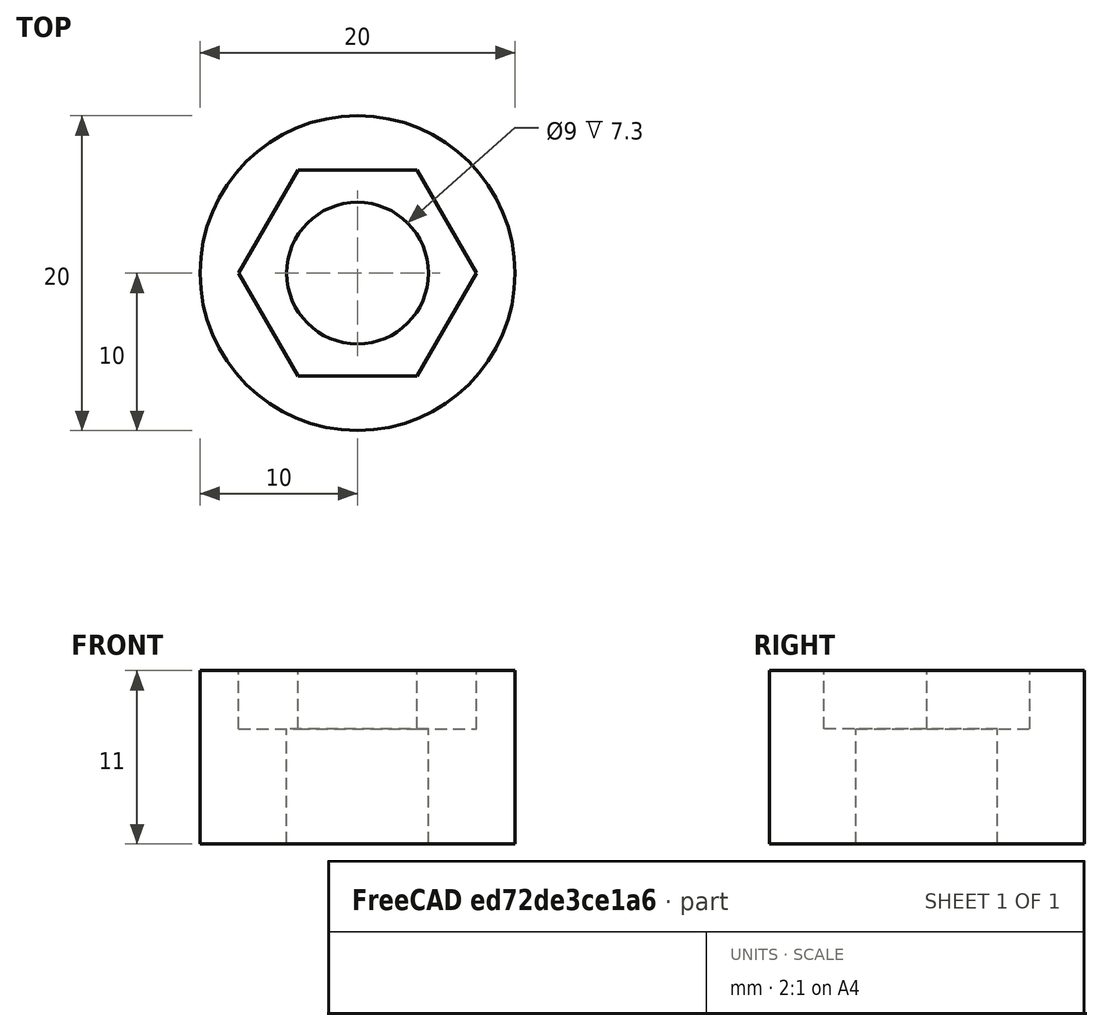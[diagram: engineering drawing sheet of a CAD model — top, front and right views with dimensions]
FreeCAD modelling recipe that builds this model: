
FCSTD DOCUMENT  (FreeCAD 0.15R4527 (Git))
Label: nut_holder
License: All rights reserved
LicenseURL: http://en.wikipedia.org/wiki/All_rights_reserved
objects: Part::Feature×2, Part::Cylinder×2, Part::Cut×2, Mesh::Feature×1, Part::Prism×1
note: 7 computed .brp shape members not serialized (recipe doc carries the construction recipe); baked Part::Feature solids carry a one-line shape summary decoded from their .brp

FEATURE [Mesh::Feature] nutholder
FEATURE [Part::Feature] nutholder001001  label="nutholder002"
  shape: bbox 20 x 20 x 11 mm, 311 faces, 0 solids (baked)
FEATURE [Part::Cylinder] Cylinder  label="Cilindro"
  Angle = 360
  Height = 7.3
  Placement = pos=(10,10,0) rot=(0,0,1;0rad)
  Radius = 4.5
FEATURE [Part::Cylinder] Cylinder001  label="Cilindro001"
  Angle = 360
  Height = 11
  Placement = pos=(10,10,0) rot=(0,0,1;0rad)
  Radius = 10
FEATURE [Part::Cut] Cut
  Base = -> Cylinder001
  Tool = -> Cylinder
FEATURE [Part::Prism] Prism  label="Prisma"
  Circumradius = 7.55
  Height = 4
  Placement = pos=(10,10,7.3) rot=(0,0,1;0rad)
  Polygon = 6
FEATURE [Part::Cut] Cut001  label="nut_holder"
  Base = -> Cut
  Tool = -> Prism
FEATURE [Part::Feature] Cut002  label="nut_holder001"
  shape: bbox 20 x 20 x 11 mm, 11 faces (baked)
